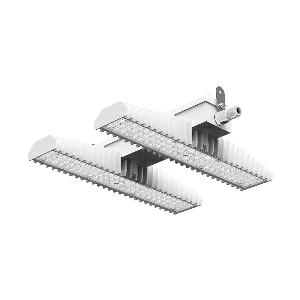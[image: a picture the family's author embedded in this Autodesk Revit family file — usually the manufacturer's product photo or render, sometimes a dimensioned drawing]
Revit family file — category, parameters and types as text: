
# Revit family: 3f_filippi_-_3f_lem_ht_ampio_3f_filippi_-_59026_-_3f_lem_2_ht_led_60_cr_ampio
name_source: partatom
category: Lighting Fixtures
units: mm (PartAtom-declared; Revit-internal decimal feet)

## family parameters
Cut with Voids When Loaded = No
Host = Face
Light Source = No
Part Type = Normal
Room Calculation Point = No
Round Connector Dimension = Use Diameter
Shared = No

## types (1)
- 3F Filippi - 3F LEM HT Ampio (1 x LED, 10869 lm, 68 W, 4000 K)
    Apparent Load = 68 VA
    Approval mark = ENEC
    CIE Flux Codes = 60 92 99 100 100
    Color Rendering = 80
    Color Temperature = 4000 K
    Control Gear = Electronic ballast
    Default Elevation = 1800 mm
    Description = Industrial luminaire with high light output and high luminous efficiency designed with the most innovative technologies for environments with temperature up to 70°C.

ILLUMINOTECHNICAL
Luminous efficiency 100% (DLOR 100%, ULOR 0%).
Initial luminous flux of the luminaire 10869 lm.
Direct symmetric wide distribution: the illuminated area has a rectangular shape.
Installation Interdistance Transv.D = 1.58 x hu - Long.D = 1.45 x hu.
Tabular UGR (CIE 117 - 4H-8H; S=0.25H; 70/50/20): RUG 20.9 - 21.9.
Beam angle: 93° - 99°.
Luminous efficacy 160 lm/W.
Lifetime (L93/B10): 30000 h. (tq+25°C)
Lifetime (L90/B10): 50000 h. (tq+25°C)
Lifetime (L85/B10): 80000 h. (tq+25°C)
Lifetime (L80/B10): 100000 h. (tq+25°C)
Lifetime (L85/B10): 50000 h. (tq+70°C)
Sudden decreased luminous flux after 50000 hours: 0% (C0).
Photobiological safety in compliance with IEC/TR 62778: RG0 risk exempt, (IEC 62471).
In compliance with IEC/EN 62722-2-1 - IEC/EN 62717 standards.
Luminous flux at +70°C: -13.5%.

SOURCE
2 Mid-Power linear LED modules 30W/840.
Energy efficiency class (UE 2019/2020 - UE 2019/2015): C.
CIE 13.3 Colour rendering index: CRI >80 (R9 <50%).
IES TM-30 Fidelity Index: Rf = 84 Rg = 95.
CCT nominal colour temperature 4000 K.
Colour initial tolerance (MacAdam): SDCM 3.

MECHANICAL
Passive modular heatsinks in die-casted aluminium, painted in white colour.
To optimize the thermal management of the LED module, the heatsinks are oversized and provided with self-cleaning of cooling fins.
Wiring body in aluminium and galvanised steel anchored solidly to the sinks and thermally separated.
3F Lens lenses with high luminous efficiency, transparent polycarbonate, fixed to the LED modules.
Fixing brackets in stainless steel.
Luminaire with limited surface temperature. - D - (EN 60598-2-24)
Dimensions: 470x542 mm, height 129 mm. Weight 8.995 kg.
IP65 protection degree.
Mechanical strength to impacts IK08 (5 joule).
Glow-wire test resistance 850°C.

ELECTRICAL
Halogen Free electronic wiring 230V-50/60Hz, power factor 0.95, THD <25%, constant output current, class I, 1 driver.
Power of the luminaire 68 W.
CE - IEC 60598-1 - EN 60598-1.
SAFE FLICKER: PstLM=<1 and SVM=<0.4 (IEC TR 61547-1 and IEC TR 63158), to ensure a more comfortable and safe light.
Luminaire compliant with EN 60598-2-22 for power supply from a centralised emergency system CPSS (Central Power Supply System), not incorporated in the luminaire - high risk areas excluded. The default power and flux are 100% in AC and 100% in DC.
Ambient temperature from -30°C to +70°C.
Temperature class T6 max 85°C.
Quick connection via M20 3P connector with 9-13 mm tightening range.
Power unit positioned on a separate compartment by the LED module to ensure optimum temperatures of cabling components, to be inspectable and maintainable.
Relative humidity UR: <85%.

INSTALLATION
Ceiling / Suspended / Wall.
All accessories dedicated to this product are available on the Catalog and on our website www.3F-Filippi.com.

APPLICATIONS
In commercial environments, exhibition and industrial areas, stores, open areas.
Applications with high ambient temperature up to 70°C.

WARNING
Fixture not suitable for cold stores with an ambient temperature <0°C and/or relative humidity >85%.
Luminaire designed for disposal/recycling at end-of-life.
Replaceable (LED only) light source by a professional. Replaceable control gear by a professional.
    Height = 129 mm
    Lamp = 1 x LED
    Lamp Light Flux = 10869 lm
    Lamp Power = 68 W
    Lamp count = 1
    Length = 470 mm
    Lifetime = 50000 h
    Luminous efficacy = 160 lm/W
    Manufacturer = 3F Filippi
    ModVariant = No
    Model = 3F Filippi - 59026 - 3F LEM 2 HT LED 60 CR AMPIO
    Mounting Place = Ceiling
    Mounting Type = Pendant
    Number of Poles = 1
    OnlyDefault = Yes
    Power Factor = 1
    Product Name = 3F Filippi - 3F LEM HT Ampio
    Product group = pendant luminaire
    ProductGroupID = 9
    Protection Class = Protection class I
    Protection Degree = IP 65
    RLX_Detail_Level = 1
    RLX_Emergency_Light_Flux = 0 lm
    RLX_Emergency_Type = 0
    RLX_Emergency_Type_DB = No
    RlxData = <blob elided: 95469 chars, md5=3a2e34e4>
    Socket = socket
    Standby Power = 0 W
    System Light Flux = 10869 lm
    System Power = 68 W
    Type Comments = Product without accessories
    Type Image = 3f_filippi_-_lem_2.jpg
    URL = http://relux.com
    VarID = ---
    Voltage = 0 V
    Weight = 0.00 kg
    Width = 542 mm

## geometry (parser evidence)
native form markers: Blend x4, Sweep x11
no freeform markers — native parametric forms only
